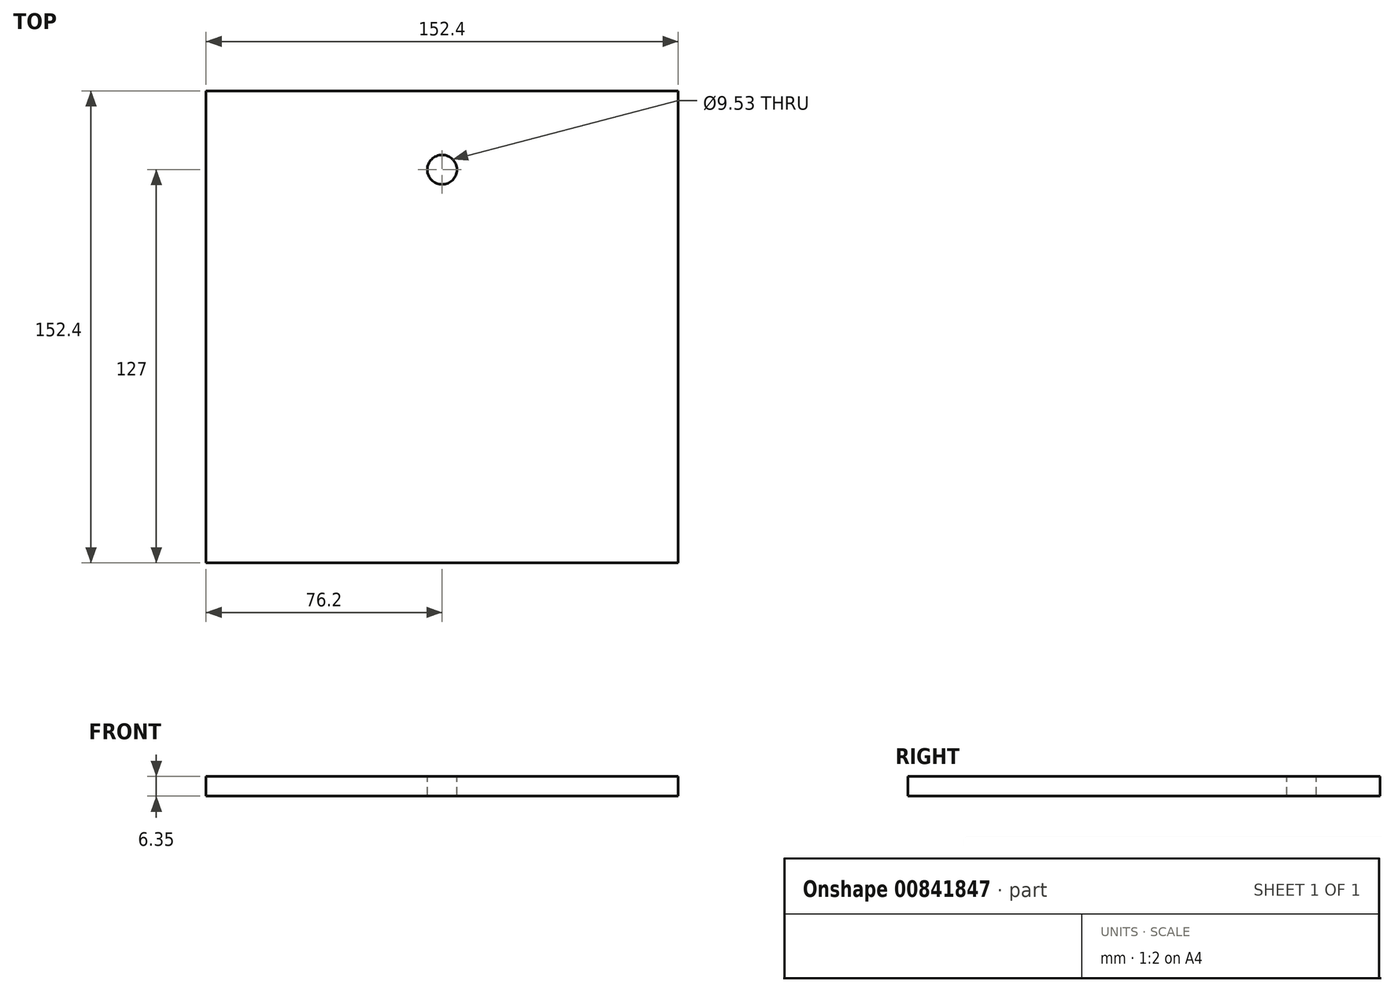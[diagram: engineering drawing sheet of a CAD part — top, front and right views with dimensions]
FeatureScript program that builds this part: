
annotation { "Feature Type Name" : "Feature", "Feature Type Description" : "" }
export const myFeature = defineFeature(function(context is Context, id is Id, definition is map)
    precondition{}
    {
        {
            var Q0;
            Q0=qCreatedBy(makeId("Top.planeOp"),FACE);
            var sketch = newSketch(context, id + "F0", { "sketchPlane" : qUnion([Q0])});
            skLineSegment(sketch, "E0.bottom", {"start": v(-76.2, 76.2) * mm, "end": v(76.2, 76.2) * mm});
            skLineSegment(sketch, "E0.top", {"start": v(-76.2, -76.2) * mm, "end": v(76.2, -76.2) * mm});
            skLineSegment(sketch, "E0.left", {"start": v(-76.2, 76.2) * mm, "end": v(-76.2, -76.2) * mm});
            skLineSegment(sketch, "E0.right", {"start": v(76.2, 76.2) * mm, "end": v(76.2, -76.2) * mm});
            skSolve(sketch);
        }
        {
            var Q0;
            Q0 = qSketchRegion(id + "F0", true);
            extrude(context, id + "F1", {"entities" : qUnion([Q0]), "depth" : 6.35 * mm, "offsetDistance" : 25.4 * mm});
        }
        {
            var Q0;
            Q0=makeQuery(id+"F1.opExtrude","CAP_FACE",FACE,{"disambiguationData":[OSD([sQuery(id+"F0.wireOp",EDGE,"E0.bottom"),sQuery(id+"F0.wireOp",EDGE,"E0.top"),sQuery(id+"F0.wireOp",EDGE,"E0.left"),sQuery(id+"F0.wireOp",EDGE,"E0.right")])],"isStart":false});
            var sketch = newSketch(context, id + "F2", { "sketchPlane" : qUnion([Q0])});
            skCircle(sketch, "E1", {"center": v(0, 50.8) * mm, "radius": 4.76 * mm});
            skSolve(sketch);
        }
        {
            var Q0;
            Q0 = qSketchRegion(id + "F2", true);
            extrude(context, id + "F3", {"entities" : qUnion([Q0]), "operationType" : NewBodyOperationType.REMOVE, "endBound" : BoundingType.THROUGH_ALL, "oppositeDirection" : true, "depth" : 25.4 * mm, "offsetDistance" : 25.4 * mm});
        }
        {
            var Q0;
            Q0=qCreatedBy(makeId("Front.planeOp"),FACE);
            var sketch = newSketch(context, id + "F4", { "sketchPlane" : qUnion([Q0])});
            skLineSegment(sketch, "E2", {"start": v(0, 44.84) * mm, "end": v(0, -54.04) * mm, "construction": true});
            skSolve(sketch);
        }
    });
